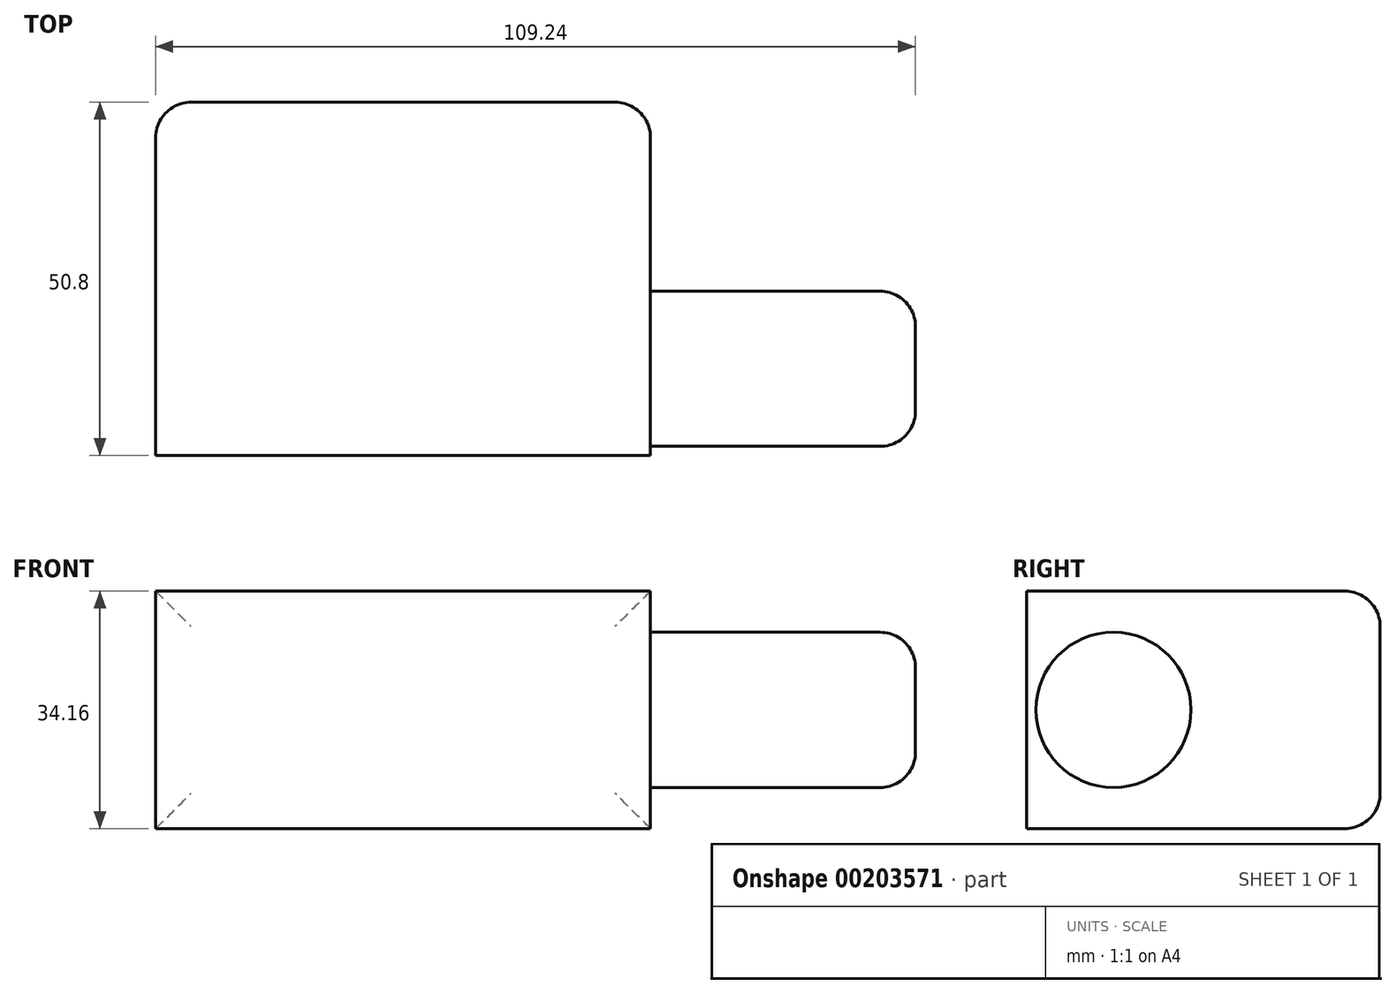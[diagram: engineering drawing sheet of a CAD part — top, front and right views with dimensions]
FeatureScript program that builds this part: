
annotation { "Feature Type Name" : "Feature", "Feature Type Description" : "" }
export const myFeature = defineFeature(function(context is Context, id is Id, definition is map)
    precondition{}
    {
        {
            var Q0;
            Q0=qCreatedBy(makeId("Front.planeOp"),FACE);
            var sketch = newSketch(context, id + "F0", { "sketchPlane" : qUnion([Q0])});
            skLineSegment(sketch, "E0.bottom", {"start": v(-35.57, 17.08) * mm, "end": v(35.57, 17.08) * mm});
            skLineSegment(sketch, "E0.top", {"start": v(-35.57, -17.08) * mm, "end": v(35.57, -17.08) * mm});
            skLineSegment(sketch, "E0.left", {"start": v(-35.57, 17.08) * mm, "end": v(-35.57, -17.08) * mm});
            skLineSegment(sketch, "E0.right", {"start": v(35.57, 17.08) * mm, "end": v(35.57, -17.08) * mm});
            skPoint(sketch, "E0.middle", {"position": v(0, 0) * mm});
            skLineSegment(sketch, "E1.bottom", {"start": v(144.54, 45.6) * mm, "end": v(66.62, 45.6) * mm});
            skLineSegment(sketch, "E1.top", {"start": v(144.54, 81.73) * mm, "end": v(66.62, 81.73) * mm});
            skLineSegment(sketch, "E1.left", {"start": v(144.54, 45.6) * mm, "end": v(144.54, 81.73) * mm});
            skLineSegment(sketch, "E1.right", {"start": v(66.62, 45.6) * mm, "end": v(66.62, 81.73) * mm});
            skPoint(sketch, "E1.middle", {"position": v(105.58, 63.66) * mm});
            skLineSegment(sketch, "E2", {"start": v(35.57, 17.08) * mm, "end": v(35.57, 47.29) * mm});
            skArc(sketch, "E3", {"start": v(35.57, 47.29) * mm, "mid": v(39.38, 56.48) * mm, "end": v(48.58, 60.3) * mm});
            skLineSegment(sketch, "E4", {"start": v(48.58, 60.3) * mm, "end": v(94.85, 60.3) * mm});
            skSolve(sketch);
        }
        {
            var Q0;
            Q0=makeQuery(id+"F0.imprint","IMPRINT",FACE,{"disambiguationData":[TD([[makeQuery(id+"F0.imprint","IMPRINT",EDGE,{"derivedFrom":sQuery(id+"F0.wireOp",EDGE,"E0.bottom")}),-1.0]])]});
            extrude(context, id + "F1", {"entities" : qUnion([Q0]), "depth" : 50.8 * mm});
        }
        {
            var Q0;
            Q0=makeQuery(id+"F1.opExtrude","SWEPT_FACE",FACE,{"disambiguationData":[OSD([sQuery(id+"F0.wireOp",EDGE,"E0.right")])]});
            var sketch = newSketch(context, id + "F2", { "sketchPlane" : qUnion([Q0])});
            skCircle(sketch, "E5", {"center": v(-38.33, 0) * mm, "radius": 11.15 * mm});
            skSolve(sketch);
        }
        {
            var Q0;
            Q0 = qSketchRegion(id + "F2", true);
            extrude(context, id + "F3", {"entities" : qUnion([Q0]), "operationType" : NewBodyOperationType.ADD, "depth" : 38.1 * mm});
        }
        {
            var Q0;
            Q0=makeQuery(id+"F3.opExtrude","CAP_EDGE",EDGE,{"disambiguationData":[OSD([sQuery(id+"F2.wireOp",EDGE,"E5")])],"isStart":true});
            var Q1;
            Q1=makeQuery(id+"F3.opExtrude","CAP_EDGE",EDGE,{"disambiguationData":[OSD([sQuery(id+"F2.wireOp",EDGE,"E5")])],"isStart":false});
            var Q2;
            Q2=makeQuery(id+"F1.opExtrude","CAP_EDGE",EDGE,{"disambiguationData":[OSD([sQuery(id+"F0.wireOp",EDGE,"E0.bottom")])],"isStart":true});
            var Q3;
            Q3=makeQuery(id+"F1.opExtrude","CAP_EDGE",EDGE,{"disambiguationData":[OSD([sQuery(id+"F0.wireOp",EDGE,"E0.top")])],"isStart":true});
            var Q4;
            Q4=makeQuery(id+"F1.opExtrude","CAP_EDGE",EDGE,{"disambiguationData":[OSD([sQuery(id+"F0.wireOp",EDGE,"E0.left")])],"isStart":true});
            var Q5;
            Q5=makeQuery(id+"F1.opExtrude","CAP_EDGE",EDGE,{"disambiguationData":[OSD([sQuery(id+"F0.wireOp",EDGE,"E0.right")])],"isStart":true});
            fillet(context, id + "F4", {"entities" : qUnion([Q0, Q1, Q2, Q3, Q4, Q5]), "radius" : 5.08 * mm, "tangentPropagation" : true, "allowEdgeOverflow" : false});
        }
    });
